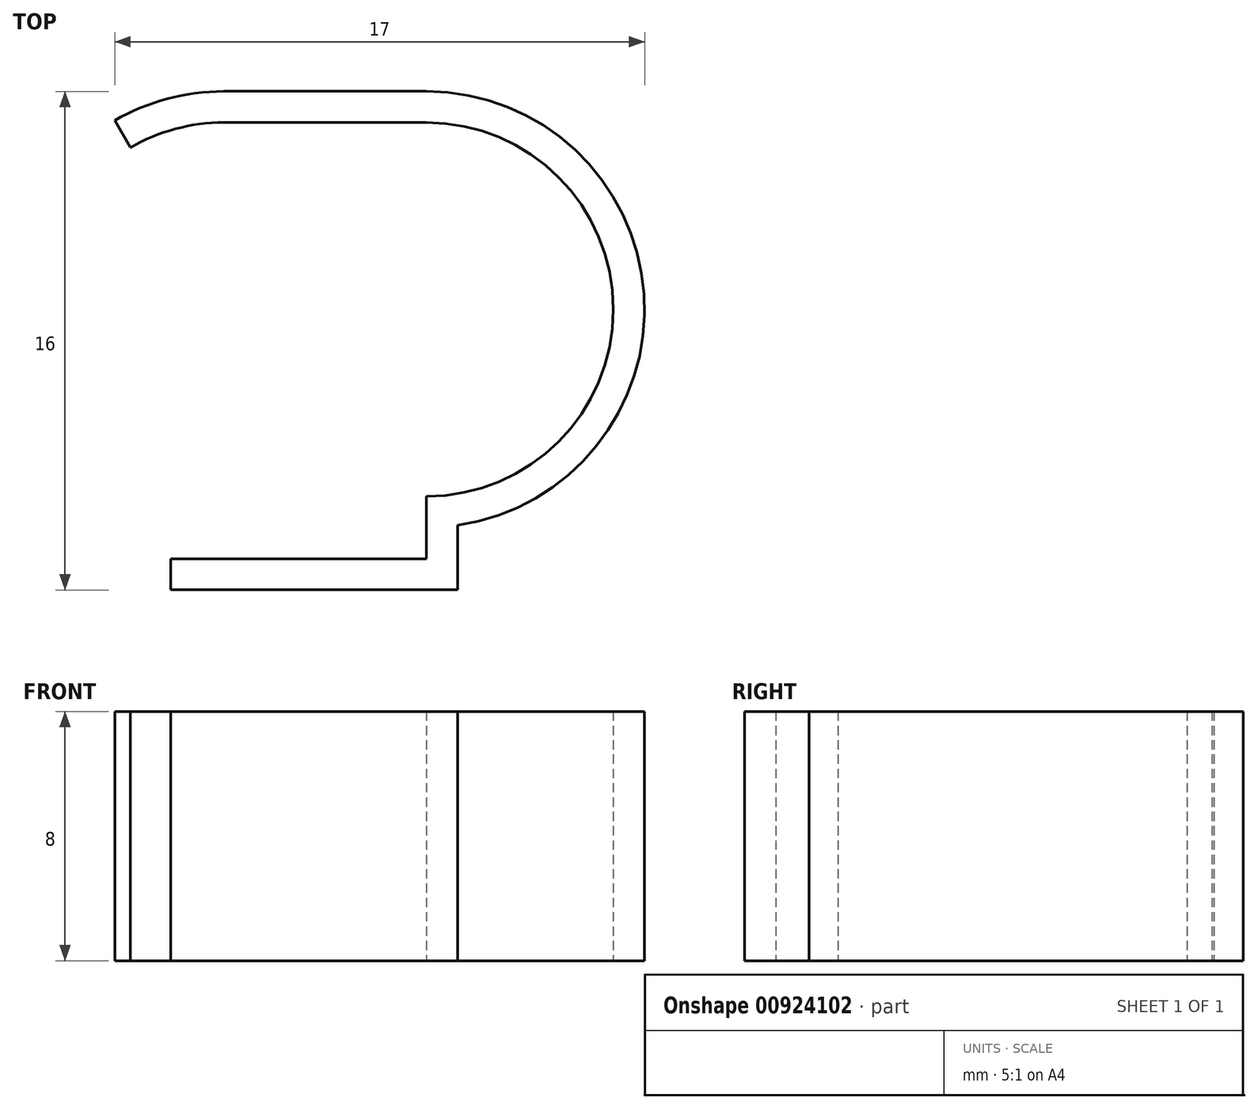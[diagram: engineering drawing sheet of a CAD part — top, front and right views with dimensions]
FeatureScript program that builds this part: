
annotation { "Feature Type Name" : "Feature", "Feature Type Description" : "" }
export const myFeature = defineFeature(function(context is Context, id is Id, definition is map)
    precondition{}
    {
        {
            var Q0;
            Q0=qCreatedBy(makeId("Top.planeOp"),FACE);
            var sketch = newSketch(context, id + "F0", { "sketchPlane" : qUnion([Q0])});
            skLineSegment(sketch, "E0.bottom", {"start": v(-6.76, -7.15) * mm, "end": v(1.44, -7.15) * mm});
            skLineSegment(sketch, "E0.top", {"start": v(-6.76, -8.15) * mm, "end": v(1.44, -8.15) * mm});
            skLineSegment(sketch, "E0.left", {"start": v(-6.76, -7.15) * mm, "end": v(-6.76, -8.15) * mm});
            skLineSegment(sketch, "E0.right", {"start": v(1.44, -7.15) * mm, "end": v(1.44, -8.15) * mm});
            skLineSegment(sketch, "E1.bottom", {"start": v(1.44, -8.15) * mm, "end": v(2.44, -8.15) * mm});
            skLineSegment(sketch, "E1.top", {"start": v(1.44, -5.15) * mm, "end": v(2.44, -5.15) * mm});
            skLineSegment(sketch, "E1.left", {"start": v(1.44, -8.15) * mm, "end": v(1.44, -5.15) * mm});
            skLineSegment(sketch, "E1.right", {"start": v(2.44, -8.15) * mm, "end": v(2.44, -5.15) * mm});
            skLineSegment(sketch, "E2", {"start": v(1.44, -10.36) * mm, "end": v(1.44, -5.15) * mm, "construction": true});
            skCircle(sketch, "E3", {"center": v(1.44, 0.85) * mm, "radius": 6 * mm});
            skCircle(sketch, "E4", {"center": v(1.44, 0.85) * mm, "radius": 7 * mm});
            skLineSegment(sketch, "E5.bottom", {"start": v(1.44, 6.85) * mm, "end": v(-5.06, 6.85) * mm});
            skLineSegment(sketch, "E5.top", {"start": v(1.44, 7.85) * mm, "end": v(-5.06, 7.85) * mm});
            skLineSegment(sketch, "E5.left", {"start": v(1.44, 6.85) * mm, "end": v(1.44, 7.85) * mm});
            skLineSegment(sketch, "E5.right", {"start": v(-5.06, 6.85) * mm, "end": v(-5.06, 7.85) * mm});
            skLineSegment(sketch, "E6", {"start": v(1.44, 0.85) * mm, "end": v(-5.06, 0.85) * mm, "construction": true});
            skCircle(sketch, "E7", {"center": v(-5.06, 0.85) * mm, "radius": 6 * mm});
            skCircle(sketch, "E8", {"center": v(-5.06, 0.85) * mm, "radius": 7 * mm});
            skLineSegment(sketch, "E9", {"start": v(-5.06, 0.85) * mm, "end": v(-8.56, 6.92) * mm});
            skLineSegment(sketch, "E10", {"start": v(-5.06, 0.85) * mm, "end": v(-5.06, 6.85) * mm, "construction": true});
            skSolve(sketch);
        }
        {
            var Q0;
            {var subQ0=sQuery(id+"F0.wireOp",EDGE,"E0.bottom");Q0=makeQuery(id+"F0.imprint","IMPRINT",FACE,{"disambiguationData":[TD([[makeQuery(id+"F0.imprint","IMPRINT",EDGE,{"derivedFrom":subQ0}),-1.0]])]});}
            var Q1;
            {var subQ4=sQuery(id+"F0.wireOp",EDGE,"E1.bottom");Q1=makeQuery(id+"F0.imprint","IMPRINT",FACE,{"disambiguationData":[TD([[makeQuery(id+"F0.imprint","IMPRINT",EDGE,{"derivedFrom":subQ4}),1.0]])]});}
            var Q2;
            {var subQ0=sQuery(id+"F0.wireOp",EDGE,"E1.top");Q2=makeQuery(id+"F0.imprint","IMPRINT",FACE,{"disambiguationData":[TD([[makeQuery(id+"F0.imprint","IMPRINT",EDGE,{"derivedFrom":subQ0}),-1.0]])]});}
            var Q3;
            {var subQ4=sQuery(id+"F0.wireOp",EDGE,"E1.top");Q3=makeQuery(id+"F0.imprint","IMPRINT",FACE,{"disambiguationData":[TD([[makeQuery(id+"F0.imprint","IMPRINT",EDGE,{"derivedFrom":subQ4}),1.0]])]});}
            var Q4;
            {var subQ0=sQuery(id+"F0.wireOp",EDGE,"E5.left");Q4=makeQuery(id+"F0.imprint","IMPRINT",FACE,{"disambiguationData":[TD([[makeQuery(id+"F0.imprint","IMPRINT",EDGE,{"derivedFrom":subQ0}),1.0]])]});}
            var Q5;
            {var subQ0=sQuery(id+"F0.wireOp",EDGE,"E5.top");Q5=makeQuery(id+"F0.imprint","IMPRINT",FACE,{"disambiguationData":[TD([[makeQuery(id+"F0.imprint","IMPRINT",EDGE,{"derivedFrom":subQ0}),1.0]])]});}
            var Q6;
            {var subQ5=sQuery(id+"F0.wireOp",EDGE,"E5.right");Q6=makeQuery(id+"F0.imprint","IMPRINT",FACE,{"disambiguationData":[TD([[makeQuery(id+"F0.imprint","IMPRINT",EDGE,{"derivedFrom":subQ5}),-1.0]])]});}
            var Q7;
            {var subQ0=sQuery(id+"F0.wireOp",EDGE,"E5.right");Q7=makeQuery(id+"F0.imprint","IMPRINT",FACE,{"disambiguationData":[TD([[makeQuery(id+"F0.imprint","IMPRINT",EDGE,{"derivedFrom":subQ0}),1.0]])]});}
            var Q8;
            {var subQ0=sQuery(id+"F0.wireOp",EDGE,"E8");var subQ1=sQuery(id+"F0.wireOp",EDGE,"E4");var subQ2=makeQuery(id+"F0.imprint","INTERSECT",VERTEX,{"disambiguationData":[OD(1.0)],"derivedFrom":[subQ1,subQ0]});Q8=makeQuery(id+"F0.imprint","IMPRINT",FACE,{"disambiguationData":[TD([[makeQuery(id+"F0.imprint","IMPRINT",EDGE,{"disambiguationData":[TD([[subQ2,-1.0]])],"derivedFrom":subQ1}),1.0]])]});}
            extrude(context, id + "F1", {"entities" : qUnion([Q0, Q1, Q2, Q3, Q4, Q5, Q6, Q7, Q8]), "depth" : 8 * mm, "offsetDistance" : 25 * mm});
        }
    });
